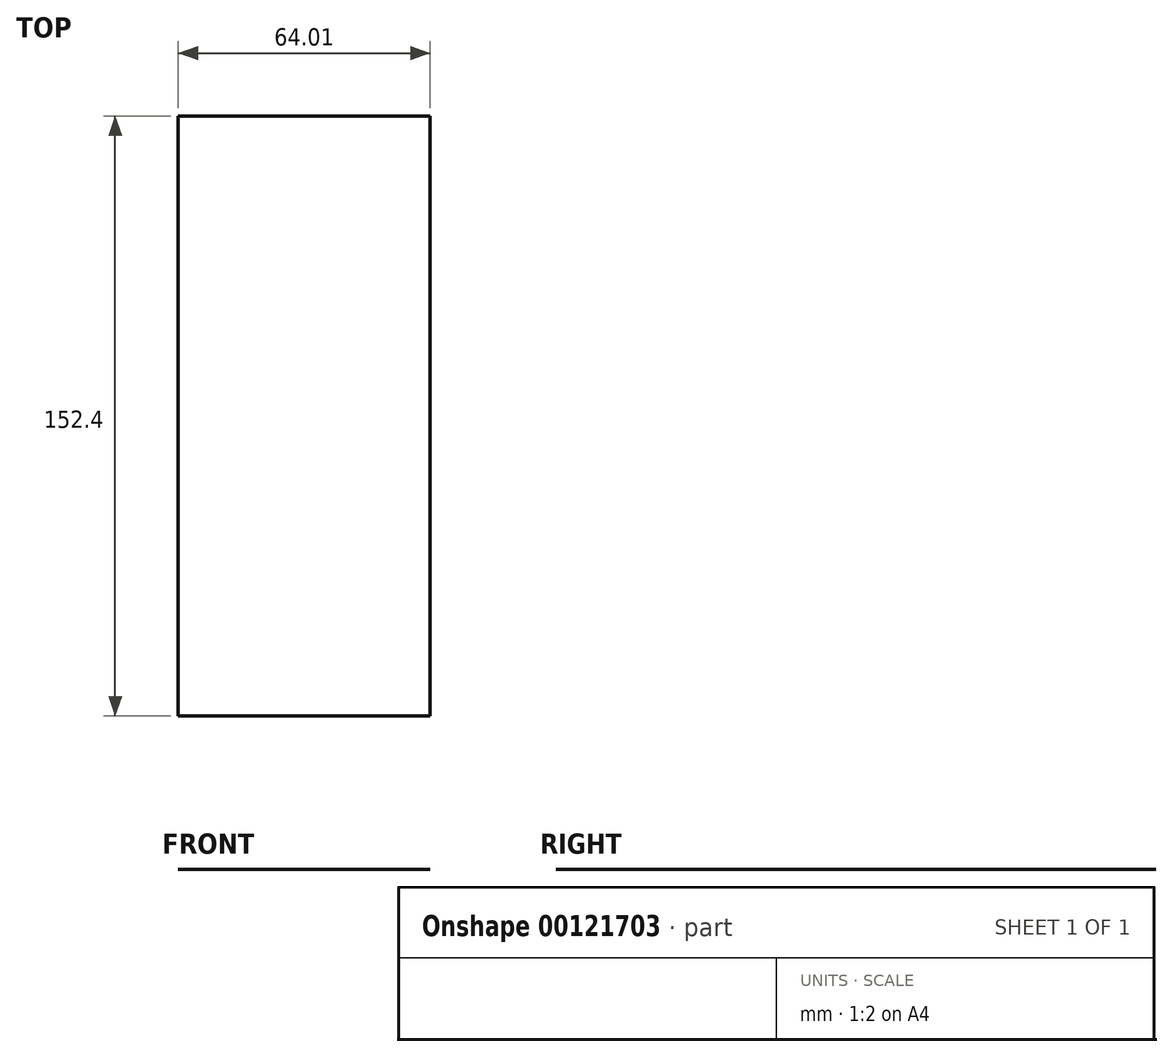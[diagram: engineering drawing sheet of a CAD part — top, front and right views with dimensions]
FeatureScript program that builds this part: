
annotation { "Feature Type Name" : "Feature", "Feature Type Description" : "" }
export const myFeature = defineFeature(function(context is Context, id is Id, definition is map)
    precondition{}
    {
        {
            var Q0;
            Q0=qCreatedBy(makeId("Front.planeOp"),FACE);
            var sketch = newSketch(context, id + "F1", { "sketchPlane" : qUnion([Q0])});
            skLineSegment(sketch, "E0.bottom", {"start": v(120.4, 166.96) * mm, "end": v(56.39, 166.96) * mm});
            skLineSegment(sketch, "E0.top", {"start": v(120.4, 98.2) * mm, "end": v(56.39, 98.2) * mm});
            skLineSegment(sketch, "E0.left", {"start": v(120.4, 166.96) * mm, "end": v(120.4, 98.2) * mm});
            skLineSegment(sketch, "E0.right", {"start": v(56.39, 166.96) * mm, "end": v(56.39, 98.2) * mm});
            skPoint(sketch, "E0.middle", {"position": v(88.4, 132.58) * mm});
            skSolve(sketch);
        }
        {
            var Q0;
            Q0=sQuery(id+"F1.wireOp",EDGE,"E0.top");
            extrude(context, id + "F0", {"bodyType" : ToolBodyType.SURFACE, "surfaceEntities" : qUnion([Q0]), "oppositeDirection" : true, "depth" : 152.4 * mm});
        }
    });
